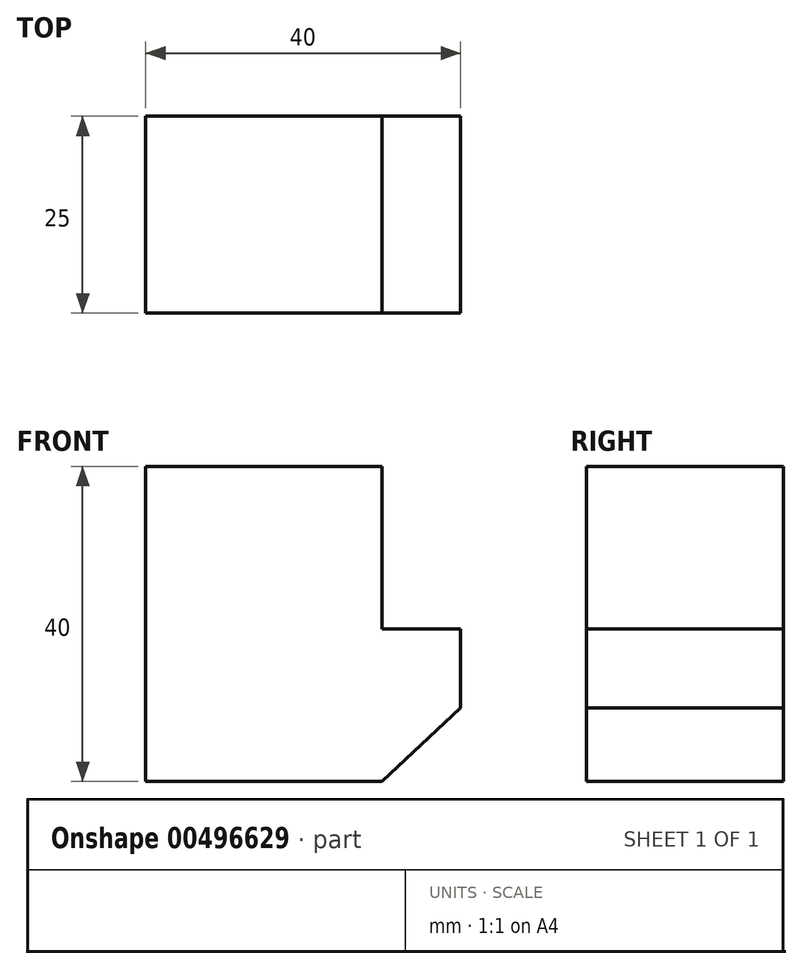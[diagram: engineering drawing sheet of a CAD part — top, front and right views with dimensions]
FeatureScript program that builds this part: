
annotation { "Feature Type Name" : "Feature", "Feature Type Description" : "" }
export const myFeature = defineFeature(function(context is Context, id is Id, definition is map)
    precondition{}
    {
        {
            var Q0;
            Q0=qCreatedBy(makeId("Front.planeOp"),FACE);
            var sketch = newSketch(context, id + "F0", { "sketchPlane" : qUnion([Q0])});
            skLineSegment(sketch, "E0", {"start": v(0, 0) * mm, "end": v(0, 30) * mm});
            skLineSegment(sketch, "E1", {"start": v(0, 0) * mm, "end": v(20, 0) * mm});
            skLineSegment(sketch, "E2", {"start": v(20, 0) * mm, "end": v(20, 9) * mm});
            skLineSegment(sketch, "E3", {"start": v(20, 9) * mm, "end": v(0, 9) * mm});
            skLineSegment(sketch, "E4", {"start": v(0, 30) * mm, "end": v(20, 30) * mm});
            skLineSegment(sketch, "E5", {"start": v(20, 30) * mm, "end": v(20, 9) * mm});
            skLineSegment(sketch, "E6", {"start": v(0, 30) * mm, "end": v(0, 40) * mm});
            skLineSegment(sketch, "E7", {"start": v(0, 40) * mm, "end": v(30, 40) * mm});
            skLineSegment(sketch, "E8", {"start": v(30, 40) * mm, "end": v(30, 19.35) * mm});
            skLineSegment(sketch, "E9", {"start": v(30, 19.35) * mm, "end": v(40, 19.35) * mm});
            skLineSegment(sketch, "E10", {"start": v(40, 19.35) * mm, "end": v(40, 9.35) * mm});
            skLineSegment(sketch, "E11", {"start": v(20, 0) * mm, "end": v(30, 0) * mm});
            skLineSegment(sketch, "E12", {"start": v(40, 9.35) * mm, "end": v(30, 0) * mm});
            skSolve(sketch);
        }
        {
            var Q0;
            {var subQ2=sQuery(id+"F0.wireOp",EDGE,"E3");Q0=makeQuery(id+"F0.imprint","IMPRINT",FACE,{"disambiguationData":[TD([[makeQuery(id+"F0.imprint","IMPRINT",EDGE,{"derivedFrom":subQ2}),-1.0]])]});}
            var Q1;
            Q1=makeQuery(id+"F0.imprint","IMPRINT",FACE,{"disambiguationData":[TD([[makeQuery(id+"F0.imprint","IMPRINT",EDGE,{"derivedFrom":sQuery(id+"F0.wireOp",EDGE,"E2")}),-1.0]])]});
            var Q2;
            {var subQ0=sQuery(id+"F0.wireOp",EDGE,"E1");Q2=makeQuery(id+"F0.imprint","IMPRINT",FACE,{"disambiguationData":[TD([[makeQuery(id+"F0.imprint","IMPRINT",EDGE,{"derivedFrom":subQ0}),1.0]])]});}
            extrude(context, id + "F1", {"entities" : qUnion([Q0, Q1, Q2]), "depth" : 25 * mm});
        }
    });
